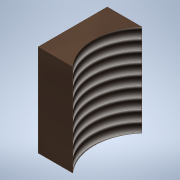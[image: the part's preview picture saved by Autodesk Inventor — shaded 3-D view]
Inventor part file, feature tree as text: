
AUTODESK INVENTOR PART (.ipt)
format: ipt  version: 2020 (Build 240168000, 168)  size: 131,072 bytes
history: native  units: in
note: dims shown in document units (in); Inventor stores cm internally (conversion verified against a paired STEP export)
features: sketch x2, extrude x2, hole x1, projected_geometry x1
ambient origin geometry x8: Origin, YZ Plane, XZ Plane, XY Plane, X Axis, Y Axis, Z Axis, Center Point
bodies: Body1 (feature_tree)
feature tree (6):
  sketch  "Sketch2"  dims[d6=1.375in d7=0.5in d8=0.0in]
  extrude  "Extrusion2"  Depth=0.5in TaperAngle=0.0deg
  hole  "Hole1"  [1 undecoded]
  extrude  "Extrusion3"  Depth=0.5in
  sketch  "Sketch3"  dims[d9=0.565in d10=1.25in d11=0.375in d12=0.25in d13=0.5635in d14=1.528in d15=0.0in d16=0.1875in d17=0.1875in d18=0.5in d19=0.0in]
  projected_geometry  "Projected Loop1"
note: 1 required parameter value undecoded (feature->parameter linkage not recoverable at this tier; creation-order binding heuristic only, values carry confidence <= 0.55)
